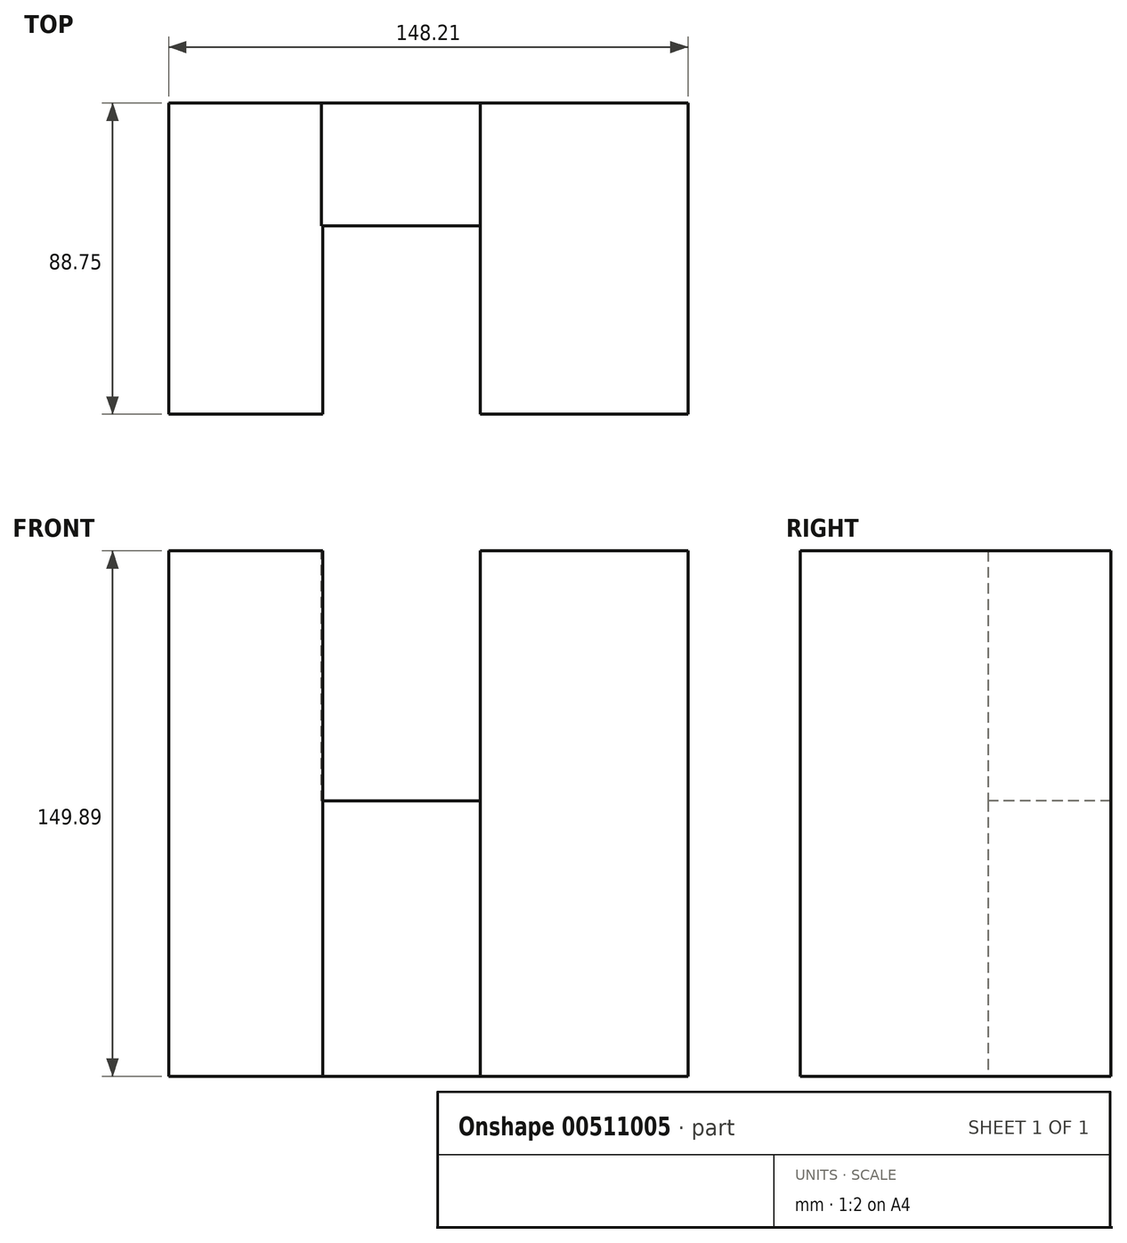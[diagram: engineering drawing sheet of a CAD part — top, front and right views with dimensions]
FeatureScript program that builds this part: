
annotation { "Feature Type Name" : "Feature", "Feature Type Description" : "" }
export const myFeature = defineFeature(function(context is Context, id is Id, definition is map)
    precondition{}
    {
        {
            var Q0;
            Q0=qCreatedBy(makeId("Front.planeOp"),FACE);
            var sketch = newSketch(context, id + "F0", { "sketchPlane" : qUnion([Q0])});
            skLineSegment(sketch, "E0.bottom", {"start": v(-88.93, 71.33) * mm, "end": v(59.28, 71.33) * mm});
            skLineSegment(sketch, "E0.top", {"start": v(-88.93, -78.56) * mm, "end": v(59.28, -78.56) * mm});
            skLineSegment(sketch, "E0.left", {"start": v(-88.93, 71.33) * mm, "end": v(-88.93, -78.56) * mm});
            skLineSegment(sketch, "E0.right", {"start": v(59.28, 71.33) * mm, "end": v(59.28, -78.56) * mm});
            skSolve(sketch);
        }
        {
            var Q0;
            Q0 = qSketchRegion(id + "F0", true);
            extrude(context, id + "F1", {"entities" : qUnion([Q0]), "depth" : 144.78 * mm});
        }
        {
            var Q0;
            Q0=makeQuery(id+"F1.opExtrude","CAP_FACE",FACE,{"disambiguationData":[OSD([sQuery(id+"F0.wireOp",EDGE,"E0.bottom"),sQuery(id+"F0.wireOp",EDGE,"E0.top"),sQuery(id+"F0.wireOp",EDGE,"E0.left"),sQuery(id+"F0.wireOp",EDGE,"E0.right")])],"isStart":false});
            var sketch = newSketch(context, id + "F2", { "sketchPlane" : qUnion([Q0])});
            skLineSegment(sketch, "E1.bottom", {"start": v(-44.97, 71.33) * mm, "end": v(0, 71.33) * mm});
            skLineSegment(sketch, "E1.top", {"start": v(-44.97, -78.56) * mm, "end": v(0, -78.56) * mm});
            skLineSegment(sketch, "E1.left", {"start": v(-44.97, 71.33) * mm, "end": v(-44.97, -78.56) * mm});
            skLineSegment(sketch, "E1.right", {"start": v(0, 71.33) * mm, "end": v(0, -78.56) * mm});
            skSolve(sketch);
        }
        {
            var Q0;
            Q0 = qSketchRegion(id + "F2", true);
            extrude(context, id + "F3", {"entities" : qUnion([Q0]), "operationType" : NewBodyOperationType.REMOVE, "oppositeDirection" : true, "depth" : 109.73 * mm});
        }
        {
            var Q0;
            Q0=makeQuery(id+"F1.opExtrude","SWEPT_FACE",FACE,{"disambiguationData":[OSD([sQuery(id+"F0.wireOp",EDGE,"E0.bottom")])]});
            var sketch = newSketch(context, id + "F4", { "sketchPlane" : qUnion([Q0])});
            skLineSegment(sketch, "E2.bottom", {"start": v(-45.29, 0) * mm, "end": v(0, 0) * mm});
            skLineSegment(sketch, "E2.top", {"start": v(-45.29, -35.05) * mm, "end": v(0, -35.05) * mm});
            skLineSegment(sketch, "E2.left", {"start": v(-45.29, 0) * mm, "end": v(-45.29, -35.05) * mm});
            skLineSegment(sketch, "E2.right", {"start": v(0, 0) * mm, "end": v(0, -35.05) * mm});
            skSolve(sketch);
        }
        {
            var Q0;
            Q0 = qSketchRegion(id + "F4", true);
            extrude(context, id + "F5", {"entities" : qUnion([Q0]), "operationType" : NewBodyOperationType.REMOVE, "oppositeDirection" : true, "depth" : 71.37 * mm});
        }
        {
            var Q0;
            Q0=makeQuery(id+"F1.opExtrude","SWEPT_FACE",FACE,{"disambiguationData":[OSD([sQuery(id+"F0.wireOp",EDGE,"E0.right")])]});
            var sketch = newSketch(context, id + "F6", { "sketchPlane" : qUnion([Q0])});
            skLineSegment(sketch, "E3.bottom", {"start": v(-144.78, 71.33) * mm, "end": v(-88.75, 71.33) * mm});
            skLineSegment(sketch, "E3.top", {"start": v(-144.78, -78.56) * mm, "end": v(-88.75, -78.56) * mm});
            skLineSegment(sketch, "E3.left", {"start": v(-144.78, 71.33) * mm, "end": v(-144.78, -78.56) * mm});
            skLineSegment(sketch, "E3.right", {"start": v(-88.75, 71.33) * mm, "end": v(-88.75, -78.56) * mm});
            skSolve(sketch);
        }
        {
            var Q0;
            Q0 = qSketchRegion(id + "F6", true);
            extrude(context, id + "F7", {"entities" : qUnion([Q0]), "operationType" : NewBodyOperationType.REMOVE, "oppositeDirection" : true, "depth" : 158.75 * mm});
        }
    });
